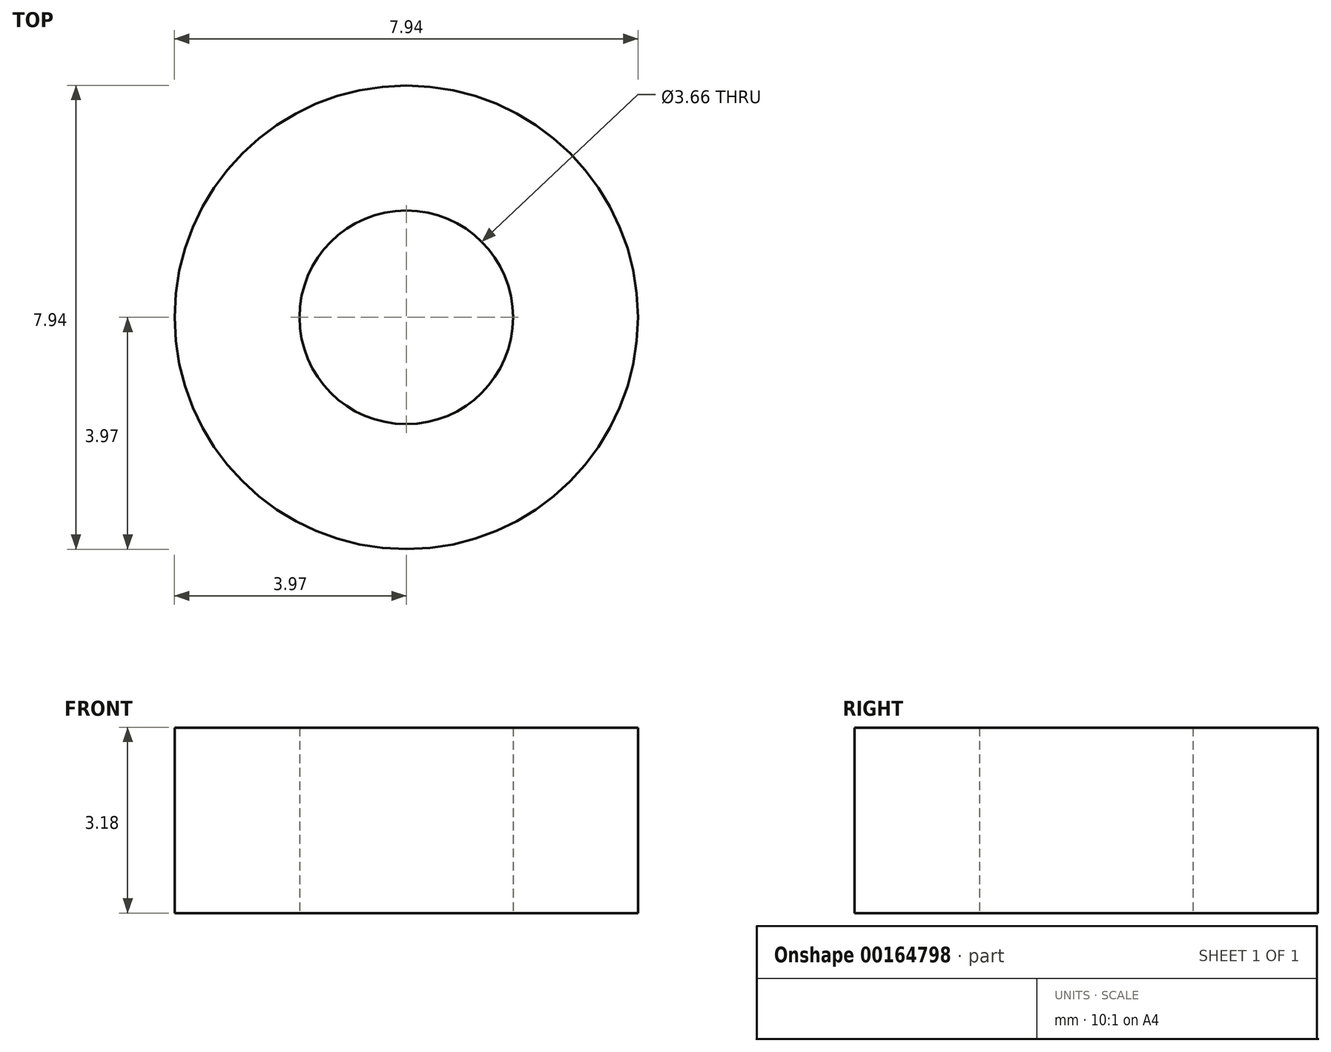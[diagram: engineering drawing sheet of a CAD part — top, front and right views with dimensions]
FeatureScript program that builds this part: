
annotation { "Feature Type Name" : "Feature", "Feature Type Description" : "" }
export const myFeature = defineFeature(function(context is Context, id is Id, definition is map)
    precondition{}
    {
        {
            var Q0;
            Q0=qCreatedBy(makeId("Top.planeOp"),FACE);
            var sketch = newSketch(context, id + "F0", { "sketchPlane" : qUnion([Q0])});
            skCircle(sketch, "E0", {"center": v(0, 0) * mm, "radius": 1.83 * mm});
            skCircle(sketch, "E1", {"center": v(0, 0) * mm, "radius": 3.97 * mm});
            skSolve(sketch);
        }
        {
            var Q0;
            Q0 = qSketchRegion(id + "F0", true);
            extrude(context, id + "F1", {"entities" : qUnion([Q0]), "depth" : 3.17 * mm});
        }
    });
